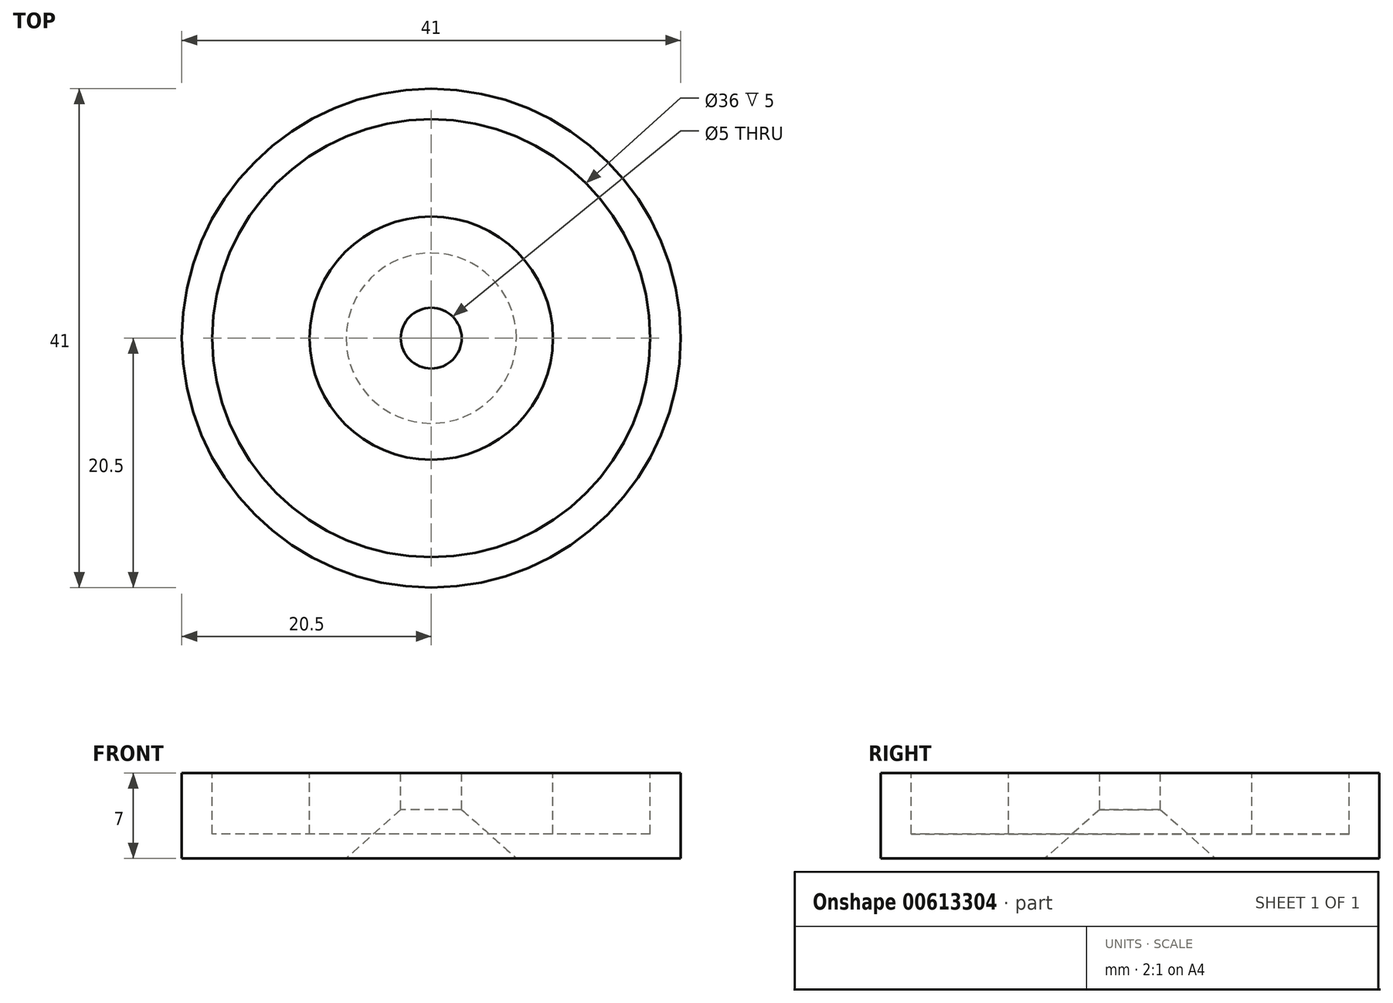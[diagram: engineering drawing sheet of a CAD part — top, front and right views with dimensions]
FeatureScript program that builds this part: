
annotation { "Feature Type Name" : "Feature", "Feature Type Description" : "" }
export const myFeature = defineFeature(function(context is Context, id is Id, definition is map)
    precondition{}
    {
        {
            var Q0;
            Q0=qCreatedBy(makeId("Top.planeOp"),FACE);
            var sketch = newSketch(context, id + "F0", { "sketchPlane" : qUnion([Q0])});
            skCircle(sketch, "E0", {"center": v(0, 0) * mm, "radius": 20.5 * mm});
            skSolve(sketch);
        }
        {
            var Q0;
            Q0 = qSketchRegion(id + "F0", true);
            extrude(context, id + "F1", {"entities" : qUnion([Q0]), "depth" : 7 * mm, "offsetDistance" : 25 * mm});
        }
        {
            var Q0;
            Q0=makeQuery(id+"F1.opExtrude","CAP_FACE",FACE,{"disambiguationData":[OSD([sQuery(id+"F0.wireOp",EDGE,"E0")])],"isStart":false});
            var sketch = newSketch(context, id + "F2", { "sketchPlane" : qUnion([Q0])});
            skCircle(sketch, "E1", {"center": v(0, 0) * mm, "radius": 18 * mm});
            skCircle(sketch, "E2", {"center": v(0, 0) * mm, "radius": 10 * mm});
            skSolve(sketch);
        }
        {
            var Q0;
            Q0 = qSketchRegion(id + "F2", true);
            extrude(context, id + "F3", {"entities" : qUnion([Q0]), "operationType" : NewBodyOperationType.REMOVE, "oppositeDirection" : true, "depth" : 5 * mm, "offsetDistance" : 25 * mm});
        }
        {
            var Q0;
            Q0=makeQuery(id+"F3.boolean.opBoolean","SPLIT",FACE,{"disambiguationData":[TD([makeQuery(id+"F3.opExtrude","SWEPT_FACE",FACE,{"disambiguationData":[OSD([sQuery(id+"F2.wireOp",EDGE,"E2")])]})])],"derivedFrom":makeQuery(id+"F1.opExtrude","CAP_FACE",FACE,{"disambiguationData":[OSD([sQuery(id+"F0.wireOp",EDGE,"E0")])],"isStart":false})});
            var sketch = newSketch(context, id + "F4", { "sketchPlane" : qUnion([Q0])});
            skCircle(sketch, "E3", {"center": v(0, 0) * mm, "radius": 2.5 * mm});
            skSolve(sketch);
        }
        {
            var Q0;
            Q0=makeQuery(id+"F4.imprint","IMPRINT",FACE,{"disambiguationData":[TD([[makeQuery(id+"F4.imprint","IMPRINT",EDGE,{"derivedFrom":sQuery(id+"F4.wireOp",EDGE,"E3")}),1.0]])]});
            extrude(context, id + "F5", {"entities" : qUnion([Q0]), "operationType" : NewBodyOperationType.REMOVE, "endBound" : BoundingType.THROUGH_ALL, "oppositeDirection" : true, "depth" : 25 * mm, "offsetDistance" : 25 * mm});
        }
        {
            var Q0;
            Q0=makeQuery(id+"F5.boolean.opBoolean","INTERSECT",EDGE,{"derivedFrom":[makeQuery(id+"F1.opExtrude","CAP_FACE",FACE,{"disambiguationData":[OSD([sQuery(id+"F0.wireOp",EDGE,"E0")])],"isStart":true}),makeQuery(id+"F5.opExtrude","SWEPT_FACE",FACE,{"disambiguationData":[OSD([sQuery(id+"F4.wireOp",EDGE,"E3")])]})]});
            chamfer(context, id + "F6", {"entities" : qUnion([Q0]), "chamferType" : ChamferType.TWO_OFFSETS, "width1" : 4.5 * mm, "oppositeDirection" : false, "width2" : 4 * mm, "tangentPropagation" : true});
        }
    });
